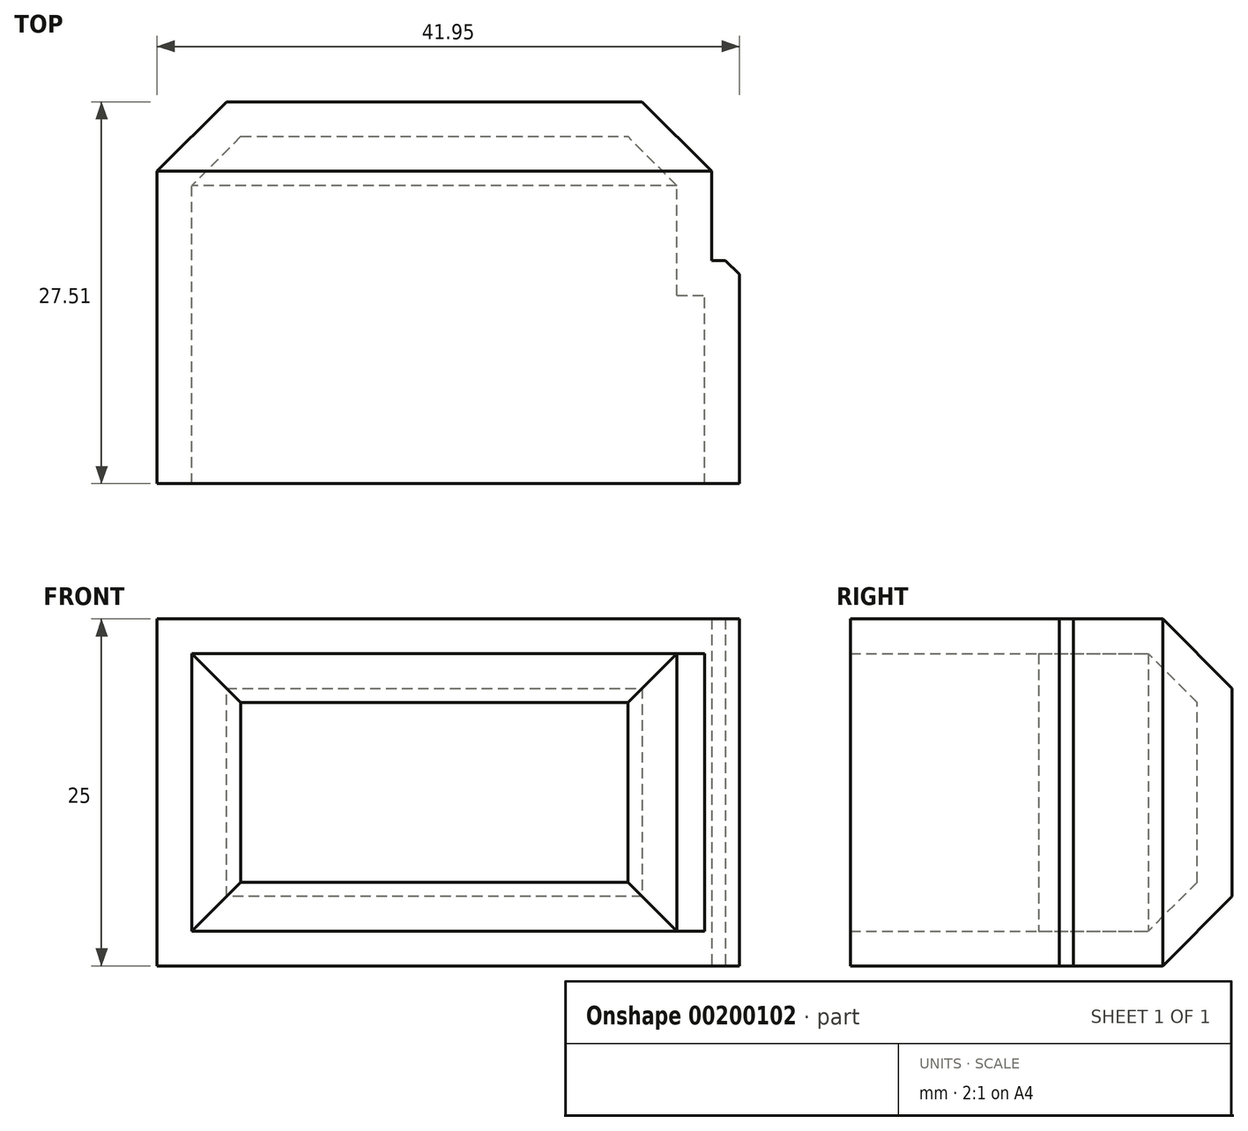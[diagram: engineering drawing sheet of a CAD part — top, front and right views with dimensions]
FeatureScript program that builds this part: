
annotation { "Feature Type Name" : "Feature", "Feature Type Description" : "" }
export const myFeature = defineFeature(function(context is Context, id is Id, definition is map)
    precondition{}
    {
        {
            var Q0;
            Q0=qCreatedBy(makeId("Top.planeOp"),FACE);
            var sketch = newSketch(context, id + "F0", { "sketchPlane" : qUnion([Q0])});
            skLineSegment(sketch, "E0.bottom", {"start": v(0, 0) * mm, "end": v(2, 0) * mm});
            skLineSegment(sketch, "E0.top", {"start": v(0, 16.07) * mm, "end": v(2, 16.07) * mm});
            skLineSegment(sketch, "E0.left", {"start": v(0, 0) * mm, "end": v(0, 16.07) * mm});
            skLineSegment(sketch, "E0.right", {"start": v(2, 0) * mm, "end": v(2, 16.07) * mm});
            skLineSegment(sketch, "E1.bottom", {"start": v(0, 0) * mm, "end": v(-17.96, 0) * mm});
            skLineSegment(sketch, "E1.top", {"start": v(0, 0) * mm, "end": v(-17.96, 0) * mm});
            skLineSegment(sketch, "E1.left", {"start": v(0, 0) * mm, "end": v(0, 0) * mm});
            skLineSegment(sketch, "E1.right", {"start": v(-17.96, 0) * mm, "end": v(-17.96, 0) * mm});
            skLineSegment(sketch, "E2.bottom", {"start": v(0, 0) * mm, "end": v(-39.95, 0) * mm});
            skLineSegment(sketch, "E2.top", {"start": v(0, 27.5) * mm, "end": v(-39.95, 27.5) * mm});
            skLineSegment(sketch, "E2.left", {"start": v(0, 0) * mm, "end": v(0, 27.5) * mm});
            skLineSegment(sketch, "E2.right", {"start": v(-39.95, 0) * mm, "end": v(-39.95, 27.5) * mm});
            skSolve(sketch);
        }
        {
            var Q0;
            Q0 = qSketchRegion(id + "F0", true);
            extrude(context, id + "F1", {"entities" : qUnion([Q0]), "depth" : 25 * mm});
        }
        {
            var Q0;
            Q0=makeQuery(id+"F1.opExtrude","SWEPT_FACE",FACE,{"disambiguationData":[OSD([sQuery(id+"F0.wireOp",EDGE,"E2.top")])]});
            chamfer(context, id + "F2", {"entities" : qUnion([Q0]), "width" : 5 * mm, "tangentPropagation" : true});
        }
        {
            var Q0;
            Q0=makeQuery(id+"F1.opExtrude","SWEPT_EDGE",EDGE,{"disambiguationData":[OSD([sQuery(id+"F0.wireOp",EDGE,"E0.top"),sQuery(id+"F0.wireOp",EDGE,"E0.right")])]});
            chamfer(context, id + "F3", {"entities" : qUnion([Q0]), "width" : 1 * mm, "tangentPropagation" : true});
        }
        {
            var Q0;
            Q0=makeQuery(id+"F1.opExtrude","SWEPT_FACE",FACE,{"disambiguationData":[OSD([sQuery(id+"F0.wireOp",EDGE,"E0.bottom"),sQuery(id+"F0.wireOp",EDGE,"E2.bottom")])]});
            shell(context, id + "F4", {"entities" : qUnion([Q0]), "thickness" : 2.5 * mm});
        }
    });
